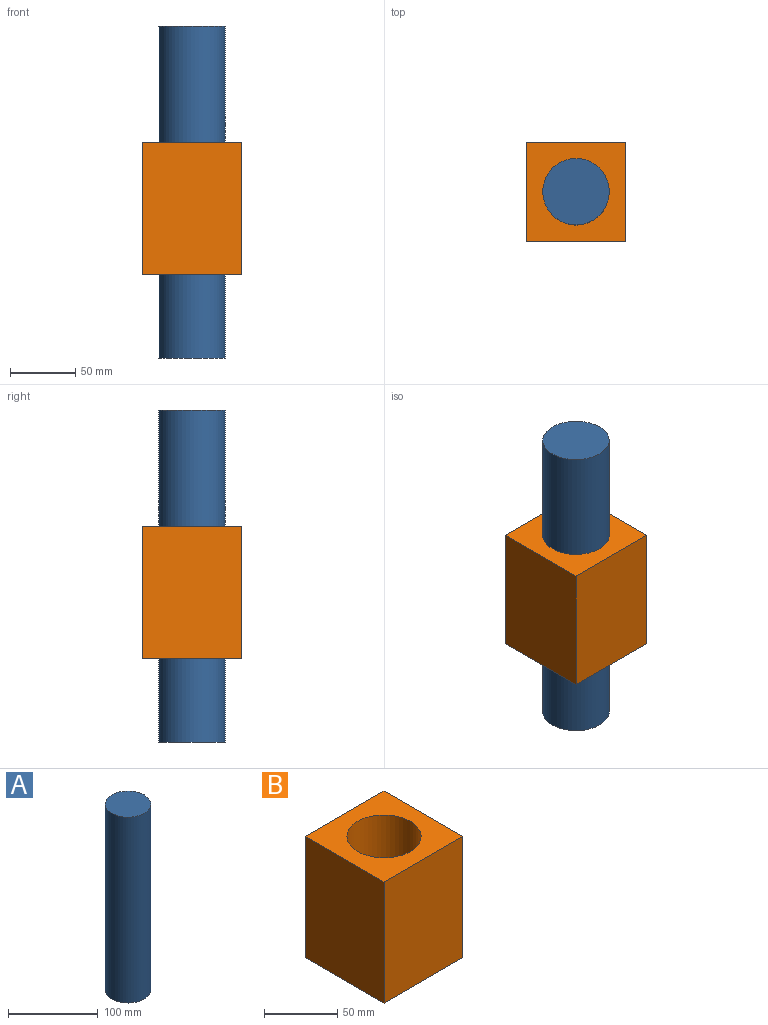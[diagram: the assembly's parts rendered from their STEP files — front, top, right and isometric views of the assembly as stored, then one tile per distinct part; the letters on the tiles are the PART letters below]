
ASSEMBLY  parts=2 mates=1
PART A: 3 faces, bbox 50.8x50.8x254 mm
  f0: cylinder r=25.4mm len=254mm, axis (0,0,1), area 40536.6mm2, adj f1,f2
  f1: plane 50.8x50.8mm, normal (0,0,-1), area 2026.8mm2, adj f0
  f2: plane 50.8x50.8mm, normal (0,0,1), area 2026.8mm2, adj f0
PART B: 7 faces, bbox 76.2x76.2x101.6 mm
  f0: plane 101.6x76.2mm, normal (0,-1,0), area 7741.9mm2, adj f1,f4,f5,f6
  f1: plane 101.6x76.2mm, normal (1,0,0), area 7741.9mm2, adj f0,f2,f5,f6
  f2: plane 101.6x76.2mm, normal (0,1,0), area 7741.9mm2, adj f1,f4,f5,f6
  f3: cylinder r=25.4mm len=101.6mm, axis (0,0,-1), area 16214.6mm2, adj f5,f6
  f4: plane 101.6x76.2mm, normal (-1,0,0), area 7741.9mm2, adj f0,f2,f5,f6
  f5: plane 76.2x76.2mm, normal (0,0,1), area 3779.6mm2, adj f0,f1,f2,f3,f4
  f6: plane 76.2x76.2mm, normal (0,0,-1), area 3779.6mm2, adj f0,f1,f2,f3,f4
PLACE A t=(168.83,79.03,208.1)mm
PLACE B t=(168.83,79.03,17.67)mm
MATE slider A.f0 <-> B.f3  axis (0,0,1) through (168.83,79.03,208.1)mm
